# Revit family: Nora Galvanised – Sunken Foundation - Without Ashtray
name_source: partatom
category: Furniture
units: mm (PartAtom-declared; Revit-internal decimal feet)

## family parameters
Always vertical = Yes
Cut with Voids When Loaded = No
OmniClass Number = 23.21.23.13.15
Room Calculation Point = No
Shared = No
Work Plane-Based = No

## types (2) — shared parameters
BIMobject category = Litter Bins
Construction material = Concrete, C12/15
Description = Sofa Sofiero Detached
Edition number = 1
IFC Classification = Furniture
Manufacturer = Hags
Manufacturer name = HAGS
OmniClass Code = 23-21 23 13 15
OmniClass Description = Residential Litter Bins
Product Guid = 90e49432-c870-4a59-897e-b15016e8f9bd
Product SKU = Nora_Detached
Product data url = https://bimobject.com
Product url = https://hags.se
QR code = https://hags.co.uk
URL = https://www.hags.com
Uniclass 1.4 Code = L8211
Uniclass 1.4 Description = Furniture
zero-valued in all types: Default Elevation

## per-type parameters (varying)
| type | Body material | Body material_90 | Model | Product name |
| 8037205 / Black | Hags - Steel - Powder coated - Black | Hags - Steel - Powder coated - Black | 8037012 | Nora – Sunken Foundation - Without Ashtray |
| 8036662 / Galvanized | Hags - Steel - Galvanized | Hags - Steel - Galvanized | 8037014 | Nora  Sunken Foundation - Without Ashtray |

## geometry (parser evidence)
native form markers: Sweep x2
no freeform markers — native parametric forms only
